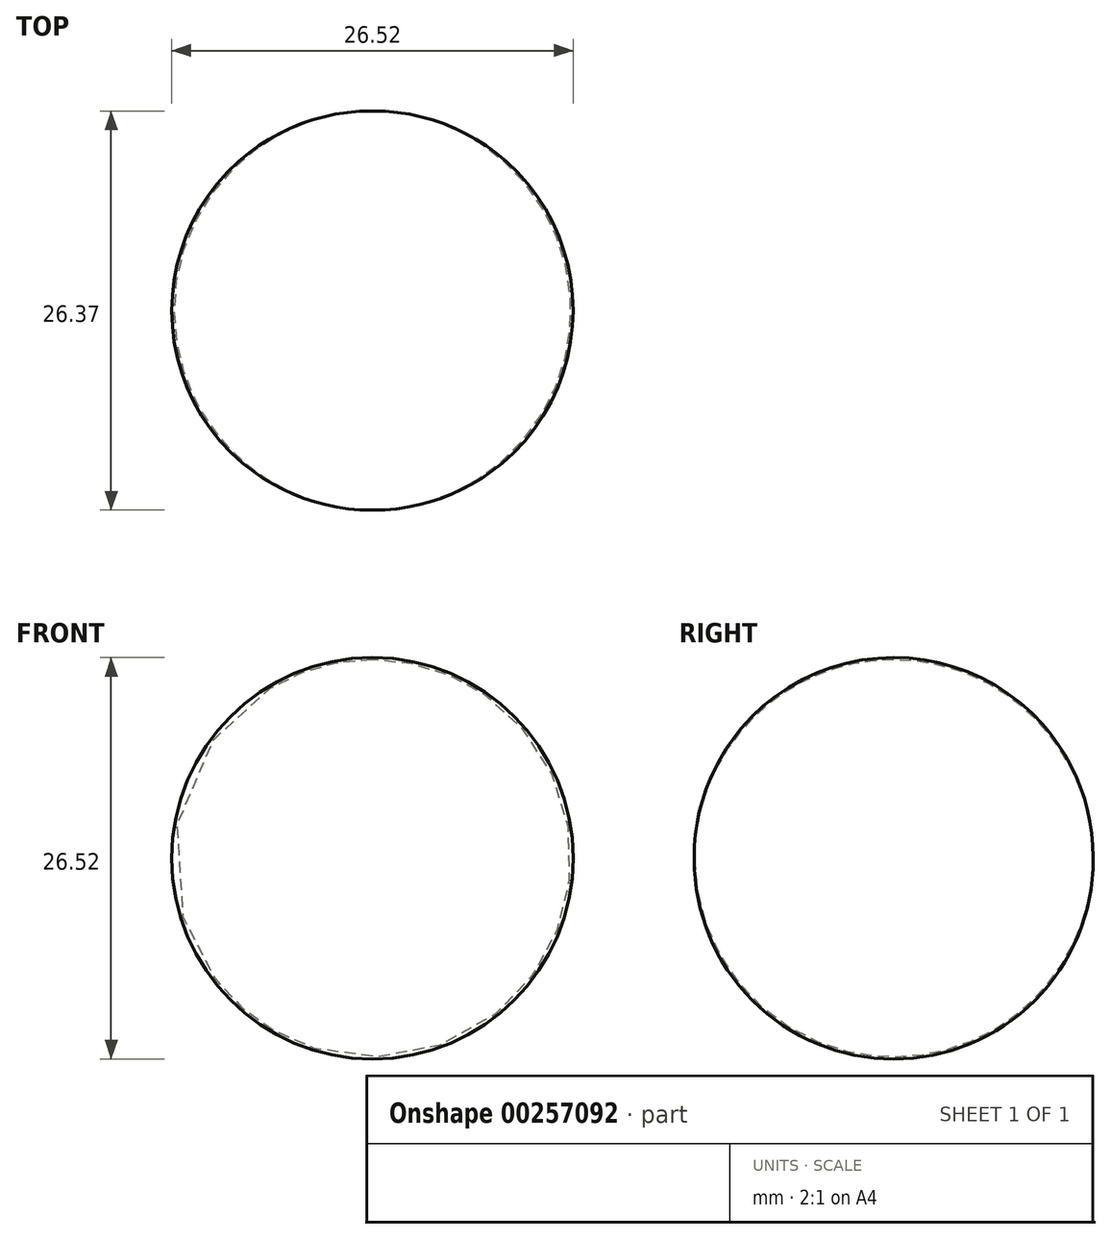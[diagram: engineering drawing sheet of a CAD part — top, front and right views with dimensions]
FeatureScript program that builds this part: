
annotation { "Feature Type Name" : "Feature", "Feature Type Description" : "" }
export const myFeature = defineFeature(function(context is Context, id is Id, definition is map)
    precondition{}
    {
        {
            var Q0;
            Q0=qCreatedBy(makeId("Top.planeOp"),FACE);
            var sketch = newSketch(context, id + "F0", { "sketchPlane" : qUnion([Q0])});
            skLineSegment(sketch, "E0", {"start": v(0, 0) * mm, "end": v(0, 26.37) * mm});
            skArc(sketch, "E1", {"start": v(0, 0) * mm, "mid": v(13.26, 13.19) * mm, "end": v(0, 26.37) * mm});
            skSolve(sketch);
        }
        {
            var Q0;
            Q0=makeQuery(id+"F0.imprint","IMPRINT",FACE,{"disambiguationData":[TD([[makeQuery(id+"F0.imprint","IMPRINT",EDGE,{"derivedFrom":sQuery(id+"F0.wireOp",EDGE,"E0")}),-1.0]])]});
            var Q1;
            Q1=sQuery(id+"F0.wireOp",EDGE,"E0");
            revolve(context, id + "F1", {"entities" : qUnion([Q0]), "axis" : qUnion([Q1]), "revolveType" : RevolveType.FULL});
        }
    });
